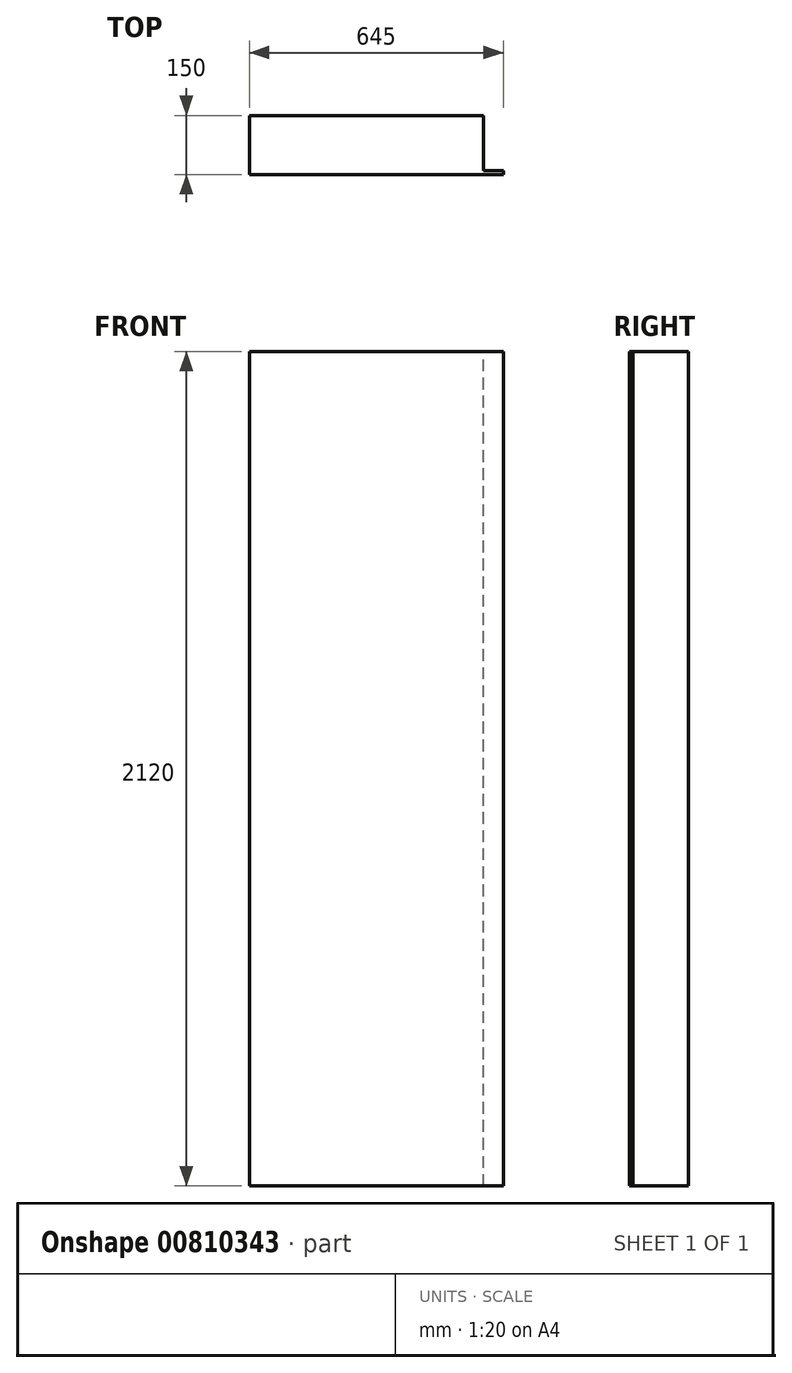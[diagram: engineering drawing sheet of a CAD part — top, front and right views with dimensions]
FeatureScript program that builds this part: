
annotation { "Feature Type Name" : "Feature", "Feature Type Description" : "" }
export const myFeature = defineFeature(function(context is Context, id is Id, definition is map)
    precondition{}
    {
        {
            var Q0;
            Q0=qCreatedBy(makeId("Top.planeOp"),FACE);
            var sketch = newSketch(context, id + "F0", { "sketchPlane" : qUnion([Q0])});
            skLineSegment(sketch, "E0.bottom", {"start": v(-322.5, 75) * mm, "end": v(322.5, 75) * mm});
            skLineSegment(sketch, "E0.top", {"start": v(-322.5, -75) * mm, "end": v(322.5, -75) * mm});
            skLineSegment(sketch, "E0.left", {"start": v(-322.5, 75) * mm, "end": v(-322.5, -75) * mm});
            skLineSegment(sketch, "E0.right", {"start": v(322.5, 75) * mm, "end": v(322.5, -75) * mm});
            skLineSegment(sketch, "E1", {"start": v(-424.04, 0) * mm, "end": v(375.03, 0) * mm, "construction": true});
            skLineSegment(sketch, "E2", {"start": v(0, 232.06) * mm, "end": v(0, -114.31) * mm, "construction": true});
            skSolve(sketch);
        }
        {
            var Q0;
            Q0 = qSketchRegion(id + "F0", true);
            extrude(context, id + "F1", {"entities" : qUnion([Q0]), "depth" : 2120 * mm, "offsetDistance" : 25.4 * mm});
        }
        {
            var Q0;
            Q0=makeQuery(id+"F1.opExtrude","CAP_FACE",FACE,{"disambiguationData":[OSD([sQuery(id+"F0.wireOp",EDGE,"E0.bottom"),sQuery(id+"F0.wireOp",EDGE,"E0.top"),sQuery(id+"F0.wireOp",EDGE,"E0.left"),sQuery(id+"F0.wireOp",EDGE,"E0.right")])],"isStart":false});
            var sketch = newSketch(context, id + "F2", { "sketchPlane" : qUnion([Q0])});
            skLineSegment(sketch, "E3", {"start": v(322.5, -65) * mm, "end": v(272.5, -65) * mm});
            skLineSegment(sketch, "E4", {"start": v(272.5, -65) * mm, "end": v(272.5, 75) * mm});
            skLineSegment(sketch, "E5", {"start": v(272.5, 75) * mm, "end": v(-322.5, 75) * mm});
            skLineSegment(sketch, "E6", {"start": v(-322.5, 75) * mm, "end": v(-322.5, -75) * mm});
            skLineSegment(sketch, "E7", {"start": v(-322.5, -75) * mm, "end": v(322.5, -75) * mm});
            skLineSegment(sketch, "E8", {"start": v(322.5, -75) * mm, "end": v(322.5, -65) * mm});
            skSolve(sketch);
        }
        {
            var Q0;
            {var subQ0=sQuery(id+"F2.wireOp",EDGE,"E3");Q0=makeQuery(id+"F2.imprint","IMPRINT",FACE,{"disambiguationData":[TD([[makeQuery(id+"F2.imprint","IMPRINT",EDGE,{"derivedFrom":subQ0}),-1.0]])]});}
            extrude(context, id + "F3", {"entities" : qUnion([Q0]), "operationType" : NewBodyOperationType.REMOVE, "endBound" : BoundingType.UP_TO_NEXT, "oppositeDirection" : true, "depth" : 25.4 * mm, "offsetDistance" : 25.4 * mm});
        }
    });
